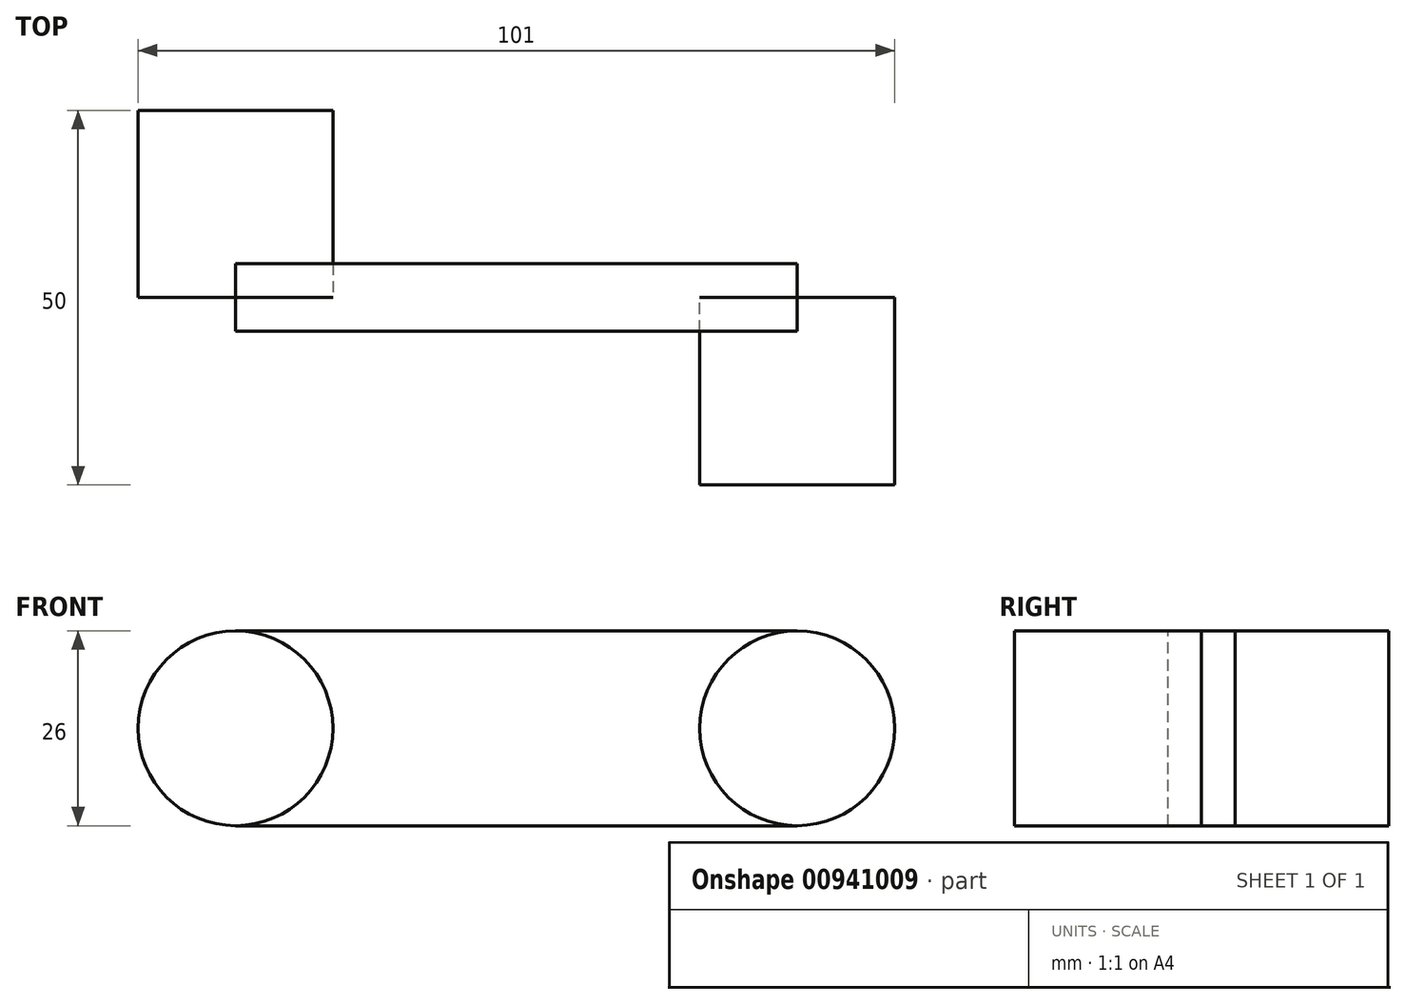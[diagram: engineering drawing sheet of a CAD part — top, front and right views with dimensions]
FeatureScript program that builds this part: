
annotation { "Feature Type Name" : "Feature", "Feature Type Description" : "" }
export const myFeature = defineFeature(function(context is Context, id is Id, definition is map)
    precondition{}
    {
        {
            var Q0;
            Q0=qCreatedBy(makeId("Front.planeOp"),FACE);
            var sketch = newSketch(context, id + "F0", { "sketchPlane" : qUnion([Q0])});
            skCircle(sketch, "E0", {"center": v(0, 0) * mm, "radius": 13 * mm});
            skLineSegment(sketch, "E1", {"start": v(0, 13) * mm, "end": v(75, 13) * mm});
            skLineSegment(sketch, "E2", {"start": v(0, -13) * mm, "end": v(75, -13) * mm});
            skCircle(sketch, "E3", {"center": v(75, 0) * mm, "radius": 13 * mm});
            skPoint(sketch, "E3.third.point", {"position": v(88, 0) * mm});
            skSolve(sketch);
        }
        {
            var Q0;
            {var subQ0=sQuery(id+"F0.wireOp",EDGE,"E0");var subQ1=makeQuery(id+"F0.imprint","INTERSECT",VERTEX,{"derivedFrom":[subQ0,sQuery(id+"F0.wireOp",EDGE,"E1")]});Q0=makeQuery(id+"F0.imprint","IMPRINT",FACE,{"disambiguationData":[TD([[makeQuery(id+"F0.imprint","IMPRINT",EDGE,{"disambiguationData":[TD([[subQ1,-1.0]])],"derivedFrom":subQ0}),1.0]])]});}
            extrude(context, id + "F1", {"entities" : qUnion([Q0]), "oppositeDirection" : true, "depth" : 25 * mm, "offsetDistance" : 25 * mm});
        }
        {
            var Q0;
            {var subQ0=sQuery(id+"F0.wireOp",EDGE,"E3");var subQ1=makeQuery(id+"F0.imprint","INTERSECT",VERTEX,{"derivedFrom":[sQuery(id+"F0.wireOp",EDGE,"E1"),subQ0]});Q0=makeQuery(id+"F0.imprint","IMPRINT",FACE,{"disambiguationData":[TD([[makeQuery(id+"F0.imprint","IMPRINT",EDGE,{"disambiguationData":[TD([[subQ1,-1.0]])],"derivedFrom":subQ0}),1.0]])]});}
            extrude(context, id + "F2", {"entities" : qUnion([Q0]), "depth" : 25 * mm, "offsetDistance" : 25 * mm});
        }
        {
            var Q0;
            {var subQ0=sQuery(id+"F0.wireOp",EDGE,"E1");Q0=makeQuery(id+"F0.imprint","IMPRINT",FACE,{"disambiguationData":[TD([[makeQuery(id+"F0.imprint","IMPRINT",EDGE,{"derivedFrom":subQ0}),-1.0]])]});}
            extrude(context, id + "F3", {"entities" : qUnion([Q0]), "endBound" : BoundingType.SYMMETRIC, "depth" : 9 * mm, "offsetDistance" : 25 * mm});
        }
    });
